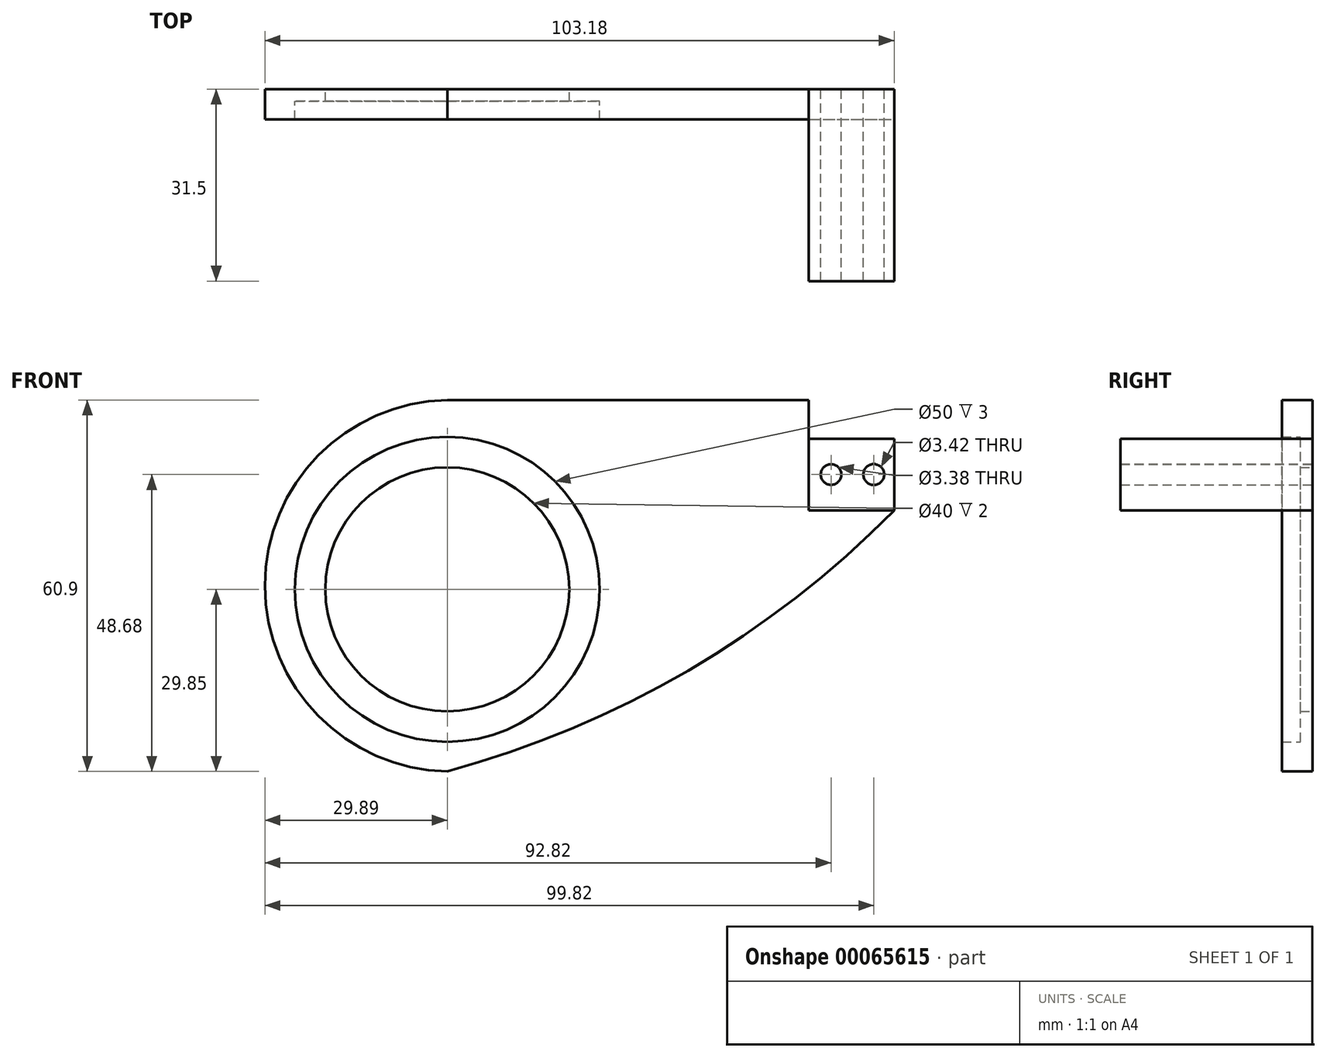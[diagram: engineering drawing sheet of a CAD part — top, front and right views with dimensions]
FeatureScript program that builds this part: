
annotation { "Feature Type Name" : "Feature", "Feature Type Description" : "" }
export const myFeature = defineFeature(function(context is Context, id is Id, definition is map)
    precondition{}
    {
        {
            var Q0;
            Q0=qCreatedBy(makeId("Front.planeOp"),FACE);
            var sketch = newSketch(context, id + "F0", { "sketchPlane" : qUnion([Q0])});
            skCircle(sketch, "E0", {"center": v(0, 0) * mm, "radius": 25 * mm});
            skCircle(sketch, "E1", {"center": v(0, 0) * mm, "radius": 17.5 * mm});
            skCircle(sketch, "E2", {"center": v(0, 0) * mm, "radius": 10 * mm});
            skCircle(sketch, "E3", {"center": v(0, 0) * mm, "radius": 5 * mm});
            skCircle(sketch, "E4", {"center": v(0, 0) * mm, "radius": 20 * mm});
            skLineSegment(sketch, "E5", {"start": v(73.29, 31.01) * mm, "end": v(59.29, 31.01) * mm});
            skLineSegment(sketch, "E6", {"start": v(59.29, 31.01) * mm, "end": v(59.29, 24.7) * mm});
            skLineSegment(sketch, "E7", {"start": v(59.29, 24.7) * mm, "end": v(73.29, 24.7) * mm});
            skLineSegment(sketch, "E8", {"start": v(73.29, 24.7) * mm, "end": v(73.29, 31.01) * mm});
            skLineSegment(sketch, "E9", {"start": v(59.29, 24.7) * mm, "end": v(59.29, 12.95) * mm});
            skLineSegment(sketch, "E10", {"start": v(59.29, 12.95) * mm, "end": v(73.29, 12.95) * mm});
            skLineSegment(sketch, "E11", {"start": v(73.29, 12.95) * mm, "end": v(73.29, 24.7) * mm});
            skCircle(sketch, "E12", {"center": v(62.93, 18.83) * mm, "radius": 1.7 * mm});
            skPoint(sketch, "E12.centerSnap0", {"position": v(59.29, 18.83) * mm});
            skCircle(sketch, "E13", {"center": v(69.93, 18.83) * mm, "radius": 1.7 * mm});
            skPoint(sketch, "E13.centerSnap0", {"position": v(73.29, 18.83) * mm});
            skLineSegment(sketch, "E14", {"start": v(0, 53.27) * mm, "end": v(0, -52.85) * mm});
            skArc(sketch, "E15", {"start": v(0, 31.05) * mm, "mid": v(-29.9, 0.6) * mm, "end": v(0, -29.85) * mm});
            skLineSegment(sketch, "E16", {"start": v(0, 31.05) * mm, "end": v(59.29, 31.01) * mm});
            skArc(sketch, "E17", {"start": v(0, -29.85) * mm, "mid": v(39.5, -13.32) * mm, "end": v(73.29, 12.95) * mm});
            skLineSegment(sketch, "E18", {"start": v(63.12, 28.96) * mm, "end": v(63.12, 26.44) * mm});
            skLineSegment(sketch, "E19", {"start": v(69.35, 28.96) * mm, "end": v(69.35, 26.44) * mm});
            skArc(sketch, "E20", {"start": v(69.35, 28.96) * mm, "mid": v(66.24, 29.82) * mm, "end": v(63.12, 28.96) * mm});
            skArc(sketch, "E21", {"start": v(63.12, 26.44) * mm, "mid": v(66.24, 25.83) * mm, "end": v(69.35, 26.44) * mm});
            skSolve(sketch);
        }
        {
            var Q0;
            {var subQ4=sQuery(id+"F0.wireOp",EDGE,"E15");Q0=makeQuery(id+"F0.imprint","IMPRINT",FACE,{"disambiguationData":[TD([[makeQuery(id+"F0.imprint","IMPRINT",EDGE,{"derivedFrom":subQ4}),1.0]])]});}
            var Q1;
            Q1=makeQuery(id+"F0.imprint","IMPRINT",FACE,{"disambiguationData":[TD([[makeQuery(id+"F0.imprint","IMPRINT",EDGE,{"derivedFrom":sQuery(id+"F0.wireOp",EDGE,"E6")}),-1.0]])]});
            extrude(context, id + "F1", {"entities" : qUnion([Q0, Q1]), "depth" : 5 * mm});
        }
        {
            var Q0;
            Q0=sQuery(id+"F0.wireOp",EDGE,"E0");
            extrude(context, id + "F2", {"bodyType" : ToolBodyType.SURFACE, "surfaceEntities" : qUnion([Q0]), "oppositeDirection" : true, "depth" : 10 * mm});
        }
        {
            var Q0;
            Q0=sQuery(id+"F0.wireOp",EDGE,"E1");
            extrude(context, id + "F3", {"bodyType" : ToolBodyType.SURFACE, "surfaceEntities" : qUnion([Q0]), "oppositeDirection" : true, "depth" : 24 * mm});
        }
        {
            var Q0;
            Q0=sQuery(id+"F0.wireOp",EDGE,"E2");
            extrude(context, id + "F4", {"bodyType" : ToolBodyType.SURFACE, "surfaceEntities" : qUnion([Q0]), "oppositeDirection" : true, "depth" : 32 * mm});
        }
        {
            var Q0;
            Q0=sQuery(id+"F0.wireOp",EDGE,"E3");
            extrude(context, id + "F5", {"bodyType" : ToolBodyType.SURFACE, "surfaceEntities" : qUnion([Q0]), "oppositeDirection" : true, "depth" : 37 * mm});
        }
        {
            var Q0;
            Q0=sQuery(id+"F0.wireOp",EDGE,"E4");
            extrude(context, id + "F6", {"bodyType" : ToolBodyType.SURFACE, "surfaceEntities" : qUnion([Q0]), "oppositeDirection" : true, "depth" : 10 * mm});
        }
        {
            var Q0;
            Q0=makeQuery(id+"F0.imprint","IMPRINT",FACE,{"disambiguationData":[TD([[makeQuery(id+"F0.imprint","IMPRINT",EDGE,{"derivedFrom":sQuery(id+"F0.wireOp",EDGE,"E7")}),-1.0]])]});
            extrude(context, id + "F7", {"entities" : qUnion([Q0]), "operationType" : NewBodyOperationType.ADD, "depth" : 31.5 * mm});
        }
        {
            var Q0;
            {var subQ0=sQuery(id+"F0.wireOp",EDGE,"E14");var subQ1=sQuery(id+"F0.wireOp",EDGE,"E0");var subQ2=makeQuery(id+"F0.imprint","INTERSECT",VERTEX,{"disambiguationData":[OD(0.0)],"derivedFrom":[subQ1,subQ0]});Q0=makeQuery(id+"F0.imprint","IMPRINT",FACE,{"disambiguationData":[TD([[makeQuery(id+"F0.imprint","IMPRINT",EDGE,{"disambiguationData":[TD([[subQ2,1.0]])],"derivedFrom":subQ1}),1.0]])]});}
            var Q1;
            {var subQ0=sQuery(id+"F0.wireOp",EDGE,"E14");var subQ1=sQuery(id+"F0.wireOp",EDGE,"E0");var subQ2=makeQuery(id+"F0.imprint","INTERSECT",VERTEX,{"disambiguationData":[OD(0.0)],"derivedFrom":[subQ1,subQ0]});Q1=makeQuery(id+"F0.imprint","IMPRINT",FACE,{"disambiguationData":[TD([[makeQuery(id+"F0.imprint","IMPRINT",EDGE,{"disambiguationData":[TD([[subQ2,-1.0]])],"derivedFrom":subQ1}),1.0]])]});}
            extrude(context, id + "F8", {"entities" : qUnion([Q0, Q1]), "operationType" : NewBodyOperationType.ADD, "depth" : 2 * mm});
        }
    });
